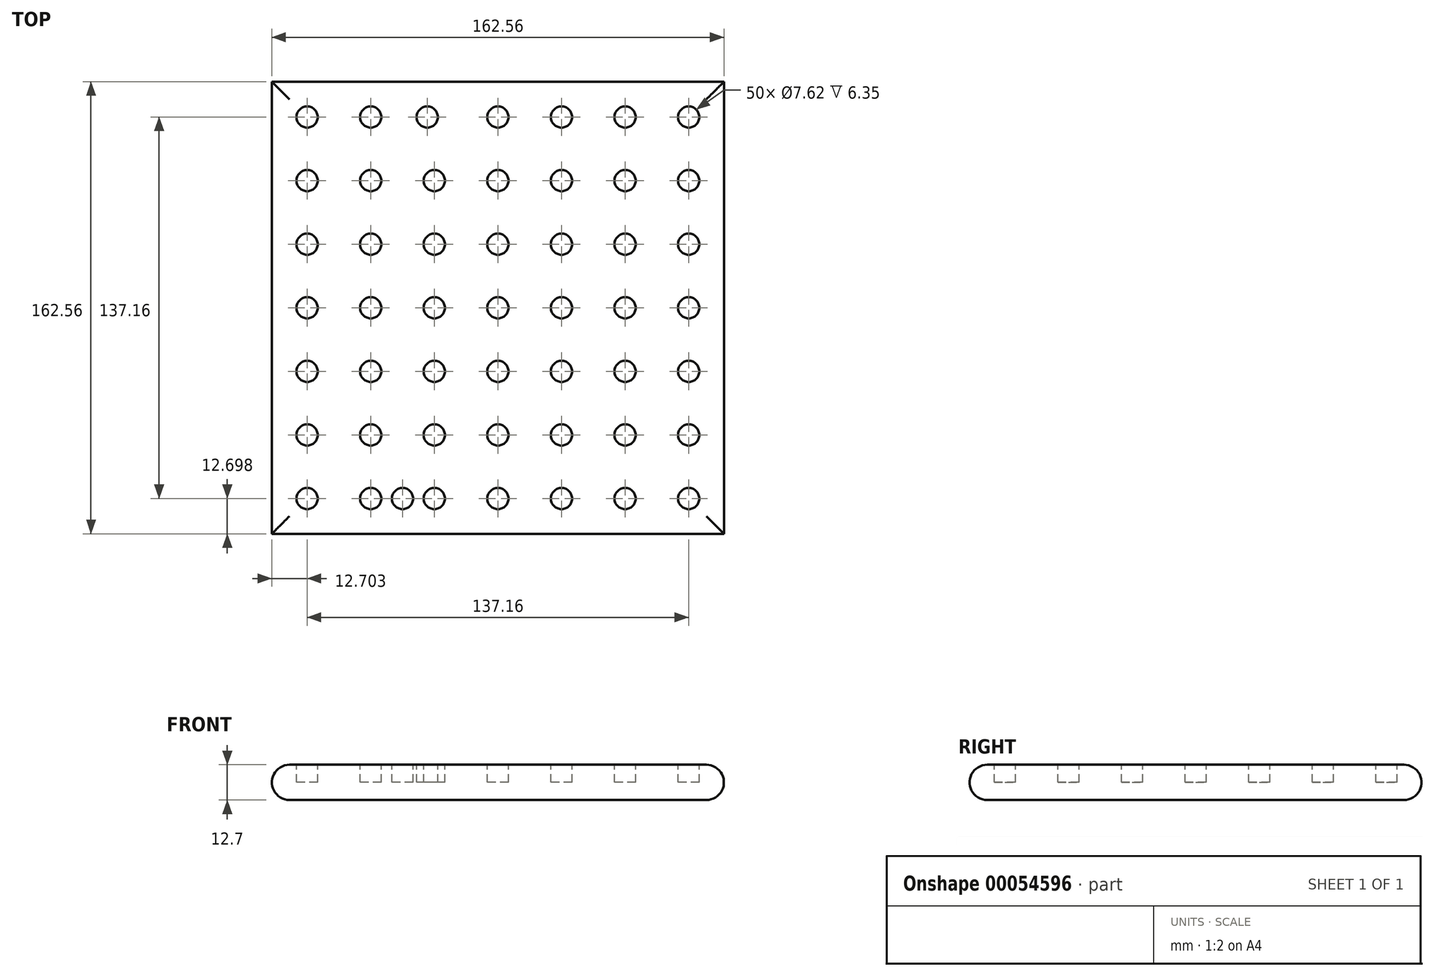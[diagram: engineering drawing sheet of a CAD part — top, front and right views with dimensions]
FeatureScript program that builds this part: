
annotation { "Feature Type Name" : "Feature", "Feature Type Description" : "" }
export const myFeature = defineFeature(function(context is Context, id is Id, definition is map)
    precondition{}
    {
        {
            var Q0;
            Q0=qCreatedBy(makeId("Top.planeOp"),FACE);
            var sketch = newSketch(context, id + "F0", { "sketchPlane" : qUnion([Q0])});
            skLineSegment(sketch, "E0.bottom", {"start": v(-144.62, 173.78) * mm, "end": v(17.94, 173.78) * mm});
            skLineSegment(sketch, "E0.top", {"start": v(-144.62, 11.22) * mm, "end": v(17.94, 11.22) * mm});
            skLineSegment(sketch, "E0.left", {"start": v(-144.62, 173.78) * mm, "end": v(-144.62, 11.22) * mm});
            skLineSegment(sketch, "E0.right", {"start": v(17.94, 173.78) * mm, "end": v(17.94, 11.22) * mm});
            skSolve(sketch);
        }
        {
            var Q0;
            Q0=qSketchRegion(id+"F0",true);
            extrude(context, id + "F1", {"entities" : qUnion([Q0]), "depth" : 12.7 * mm});
        }
        {
            var Q0;
            Q0=makeQuery(id+"F1.opExtrude","CAP_FACE",FACE,{"disambiguationData":[OSD([sQuery(id+"F0.wireOp",EDGE,"E0.bottom"),sQuery(id+"F0.wireOp",EDGE,"E0.top"),sQuery(id+"F0.wireOp",EDGE,"E0.left"),sQuery(id+"F0.wireOp",EDGE,"E0.right")])],"isStart":false});
            var sketch = newSketch(context, id + "F2", { "sketchPlane" : qUnion([Q0])});
            skSolve(sketch);
        }
        {
            var Q0;
            Q0=makeQuery(id+"F2.imprint","IMPRINT",FACE,{"disambiguationData":[TD([[makeQuery(id+"F2.imprint","IMPRINT",EDGE,{"derivedFrom":makeQuery(id+"F1.opExtrude","CAP_EDGE",EDGE,{"disambiguationData":[OSD([sQuery(id+"F0.wireOp",EDGE,"E0.bottom")])],"isStart":false})}),-1.0]])]});
            var sketch = newSketch(context, id + "F3", { "sketchPlane" : qUnion([Q0])});
            skCircle(sketch, "E1", {"center": v(-131.92, 23.92) * mm, "radius": 3.81 * mm});
            skCircle(sketch, "E2", {"center": v(-86.2, 23.92) * mm, "radius": 3.81 * mm});
            skCircle(sketch, "E3", {"center": v(-40.48, 23.92) * mm, "radius": 3.81 * mm});
            skCircle(sketch, "E4", {"center": v(5.24, 23.92) * mm, "radius": 3.81 * mm});
            skCircle(sketch, "E5", {"center": v(-109.06, 23.92) * mm, "radius": 3.81 * mm});
            skCircle(sketch, "E6", {"center": v(-63.34, 23.92) * mm, "radius": 3.81 * mm});
            skCircle(sketch, "E7", {"center": v(-17.62, 23.92) * mm, "radius": 3.81 * mm});
            skCircle(sketch, "E8", {"center": v(-131.92, 46.78) * mm, "radius": 3.81 * mm});
            skCircle(sketch, "E9", {"center": v(-131.92, 69.64) * mm, "radius": 3.81 * mm});
            skCircle(sketch, "E10", {"center": v(-131.92, 92.5) * mm, "radius": 3.81 * mm});
            skCircle(sketch, "E11", {"center": v(-131.92, 115.36) * mm, "radius": 3.81 * mm});
            skCircle(sketch, "E12", {"center": v(-131.92, 138.22) * mm, "radius": 3.81 * mm});
            skCircle(sketch, "E13", {"center": v(-131.92, 161.08) * mm, "radius": 3.81 * mm});
            skCircle(sketch, "E14", {"center": v(-109.06, 46.78) * mm, "radius": 3.81 * mm});
            skCircle(sketch, "E15", {"center": v(-109.06, 69.64) * mm, "radius": 3.81 * mm});
            skCircle(sketch, "E16", {"center": v(-109.06, 92.5) * mm, "radius": 3.81 * mm});
            skCircle(sketch, "E17", {"center": v(-109.06, 115.36) * mm, "radius": 3.81 * mm});
            skCircle(sketch, "E18", {"center": v(-109.06, 138.22) * mm, "radius": 3.81 * mm});
            skCircle(sketch, "E19", {"center": v(-109.06, 161.08) * mm, "radius": 3.81 * mm});
            skCircle(sketch, "E20", {"center": v(-86.2, 46.78) * mm, "radius": 3.81 * mm});
            skCircle(sketch, "E21", {"center": v(-63.34, 46.78) * mm, "radius": 3.81 * mm});
            skCircle(sketch, "E22", {"center": v(-40.48, 46.78) * mm, "radius": 3.81 * mm});
            skCircle(sketch, "E23", {"center": v(188.12, 46.78) * mm, "radius": 3.81 * mm});
            skCircle(sketch, "E24", {"center": v(5.24, 46.78) * mm, "radius": 3.81 * mm});
            skCircle(sketch, "E25", {"center": v(-17.62, 46.78) * mm, "radius": 3.81 * mm});
            skCircle(sketch, "E26", {"center": v(-88.74, 161.08) * mm, "radius": 3.81 * mm});
            skCircle(sketch, "E27", {"center": v(-86.2, 138.22) * mm, "radius": 3.81 * mm});
            skCircle(sketch, "E28", {"center": v(-86.2, 115.36) * mm, "radius": 3.81 * mm});
            skCircle(sketch, "E29", {"center": v(-86.2, 92.5) * mm, "radius": 3.81 * mm});
            skCircle(sketch, "E30", {"center": v(-86.2, 69.64) * mm, "radius": 3.81 * mm});
            skCircle(sketch, "E31", {"center": v(-63.34, 69.64) * mm, "radius": 3.81 * mm});
            skCircle(sketch, "E32", {"center": v(-40.48, 69.64) * mm, "radius": 3.81 * mm});
            skCircle(sketch, "E33", {"center": v(-17.62, 69.64) * mm, "radius": 3.81 * mm});
            skCircle(sketch, "E34", {"center": v(5.24, 69.64) * mm, "radius": 3.81 * mm});
            skCircle(sketch, "E35", {"center": v(-63.34, 92.5) * mm, "radius": 3.81 * mm});
            skCircle(sketch, "E36", {"center": v(-40.48, 92.5) * mm, "radius": 3.81 * mm});
            skCircle(sketch, "E37", {"center": v(-17.62, 92.5) * mm, "radius": 3.81 * mm});
            skCircle(sketch, "E38", {"center": v(5.24, 92.5) * mm, "radius": 3.81 * mm});
            skCircle(sketch, "E39", {"center": v(-17.62, 161.08) * mm, "radius": 3.81 * mm});
            skCircle(sketch, "E40", {"center": v(-63.34, 115.36) * mm, "radius": 3.81 * mm});
            skCircle(sketch, "E41", {"center": v(-63.34, 161.08) * mm, "radius": 3.81 * mm});
            skCircle(sketch, "E42", {"center": v(-17.62, 138.22) * mm, "radius": 3.81 * mm});
            skCircle(sketch, "E43", {"center": v(-40.48, 138.22) * mm, "radius": 3.81 * mm});
            skCircle(sketch, "E44", {"center": v(-40.48, 161.08) * mm, "radius": 3.81 * mm});
            skCircle(sketch, "E45", {"center": v(5.24, 115.36) * mm, "radius": 3.81 * mm});
            skCircle(sketch, "E46", {"center": v(5.24, 138.22) * mm, "radius": 3.81 * mm});
            skCircle(sketch, "E47", {"center": v(-40.48, 115.36) * mm, "radius": 3.81 * mm});
            skCircle(sketch, "E48", {"center": v(-63.34, 138.22) * mm, "radius": 3.81 * mm});
            skCircle(sketch, "E49", {"center": v(5.24, 161.08) * mm, "radius": 3.81 * mm});
            skCircle(sketch, "E50", {"center": v(-17.62, 115.36) * mm, "radius": 3.81 * mm});
            skSolve(sketch);
        }
        {
            var Q0;
            Q0=qSketchRegion(id+"F3",true);
            extrude(context, id + "F4", {"entities" : qUnion([Q0]), "operationType" : NewBodyOperationType.REMOVE, "oppositeDirection" : true, "depth" : 6.35 * mm});
        }
        {
            var Q0;
            Q0=makeQuery(id+"F1.opExtrude","CAP_EDGE",EDGE,{"disambiguationData":[OSD([sQuery(id+"F0.wireOp",EDGE,"E0.left")])],"isStart":false});
            var Q1;
            Q1=makeQuery(id+"F1.opExtrude","CAP_EDGE",EDGE,{"disambiguationData":[OSD([sQuery(id+"F0.wireOp",EDGE,"E0.left")])],"isStart":true});
            var Q2;
            Q2=makeQuery(id+"F1.opExtrude","CAP_EDGE",EDGE,{"disambiguationData":[OSD([sQuery(id+"F0.wireOp",EDGE,"E0.bottom")])],"isStart":false});
            var Q3;
            Q3=makeQuery(id+"F1.opExtrude","CAP_EDGE",EDGE,{"disambiguationData":[OSD([sQuery(id+"F0.wireOp",EDGE,"E0.bottom")])],"isStart":true});
            var Q4;
            Q4=makeQuery(id+"F1.opExtrude","CAP_EDGE",EDGE,{"disambiguationData":[OSD([sQuery(id+"F0.wireOp",EDGE,"E0.top")])],"isStart":false});
            var Q5;
            Q5=makeQuery(id+"F1.opExtrude","CAP_EDGE",EDGE,{"disambiguationData":[OSD([sQuery(id+"F0.wireOp",EDGE,"E0.top")])],"isStart":true});
            var Q6;
            Q6=makeQuery(id+"F1.opExtrude","CAP_EDGE",EDGE,{"disambiguationData":[OSD([sQuery(id+"F0.wireOp",EDGE,"E0.right")])],"isStart":false});
            var Q7;
            Q7=makeQuery(id+"F1.opExtrude","CAP_EDGE",EDGE,{"disambiguationData":[OSD([sQuery(id+"F0.wireOp",EDGE,"E0.right")])],"isStart":true});
            fillet(context, id + "F5", {"entities" : qUnion([Q0, Q1, Q2, Q3, Q4, Q5, Q6, Q7]), "radius" : 6.35 * mm, "tangentPropagation" : true, "allowEdgeOverflow" : false});
        }
        {
            var Q0;
            Q0=makeQuery(id+"F2.imprint","IMPRINT",FACE,{"disambiguationData":[TD([[makeQuery(id+"F2.imprint","IMPRINT",EDGE,{"derivedFrom":makeQuery(id+"F1.opExtrude","CAP_EDGE",EDGE,{"disambiguationData":[OSD([sQuery(id+"F0.wireOp",EDGE,"E0.bottom")])],"isStart":false})}),-1.0]])]});
            var sketch = newSketch(context, id + "F6", { "sketchPlane" : qUnion([Q0])});
            skCircle(sketch, "E51", {"center": v(-97.63, 23.92) * mm, "radius": 3.81 * mm});
            skSolve(sketch);
        }
        {
            var Q0;
            Q0 = qSketchRegion(id + "F6", true);
            extrude(context, id + "F7", {"entities" : qUnion([Q0]), "operationType" : NewBodyOperationType.REMOVE, "oppositeDirection" : true, "depth" : 6.35 * mm});
        }
    });
